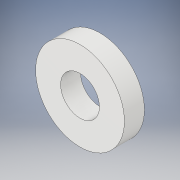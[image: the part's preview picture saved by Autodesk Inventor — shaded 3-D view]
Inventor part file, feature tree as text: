
AUTODESK INVENTOR PART (.ipt)
format: ipt  version: 2017 SP1 (Build 210196100, 196)  size: 107,008 bytes
history: native  units: in
note: dims shown in document units (in); Inventor stores cm internally (conversion verified against a paired STEP export)
features: extrude x1, sketch x1
ambient origin geometry x8: Origin, YZ Plane, XZ Plane, XY Plane, X Axis, Y Axis, Z Axis, Center Point
bodies: Solid1 (feature_tree)
feature tree (2):
  extrude  "Extrusion1"  Depth=0.0709in
  sketch  "Sketch1"  dims[d0=0.1378in d1=0.315in d2=0.0709in d3=0.0in]
